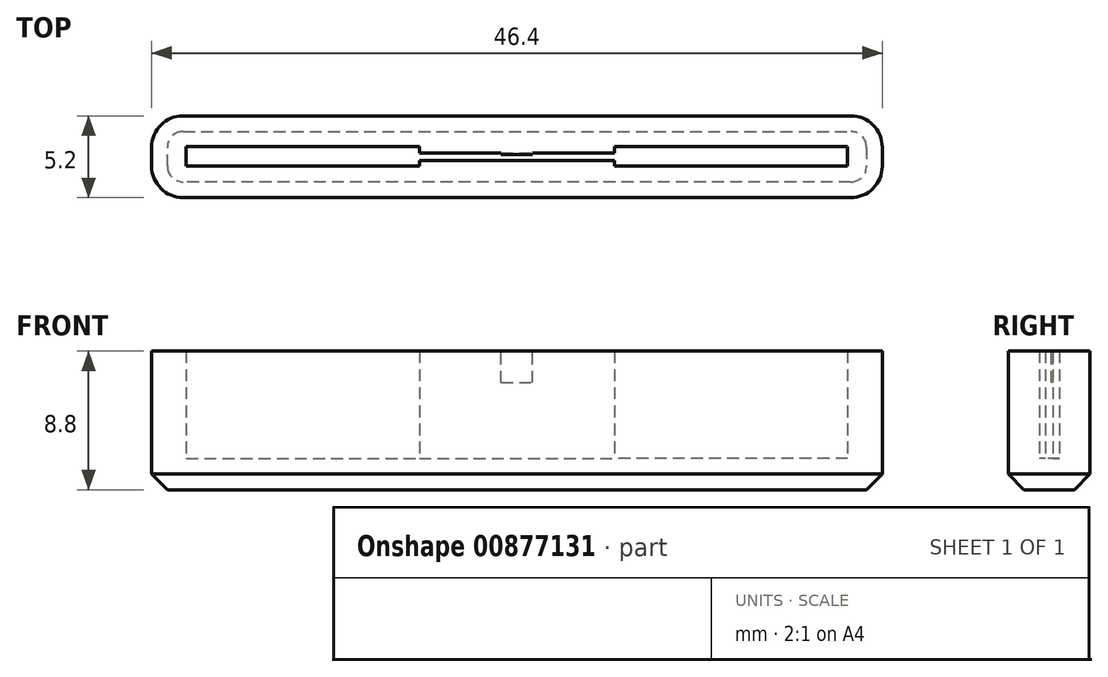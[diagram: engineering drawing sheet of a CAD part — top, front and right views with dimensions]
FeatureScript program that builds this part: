
annotation { "Feature Type Name" : "Feature", "Feature Type Description" : "" }
export const myFeature = defineFeature(function(context is Context, id is Id, definition is map)
    precondition{}
    {
        {
            var Q0;
            Q0=qCreatedBy(makeId("Top.planeOp"),FACE);
            var sketch = newSketch(context, id + "F0", { "sketchPlane" : qUnion([Q0])});
            skLineSegment(sketch, "E0.bottom", {"start": v(-23.2, 0) * mm, "end": v(23.2, 0) * mm});
            skLineSegment(sketch, "E0.top", {"start": v(-23.2, -5.2) * mm, "end": v(23.2, -5.2) * mm});
            skLineSegment(sketch, "E0.left", {"start": v(-23.2, 0) * mm, "end": v(-23.2, -5.2) * mm});
            skLineSegment(sketch, "E0.right", {"start": v(23.2, 0) * mm, "end": v(23.2, -5.2) * mm});
            skLineSegment(sketch, "E1", {"start": v(-23.2, -2.6) * mm, "end": v(23.2, -2.6) * mm, "construction": true});
            skLineSegment(sketch, "E2.left", {"start": v(-21, -2.35) * mm, "end": v(-21, -2.85) * mm});
            skLineSegment(sketch, "E2.right", {"start": v(21, -2.35) * mm, "end": v(21, -2.85) * mm});
            skPoint(sketch, "E3", {"position": v(0, -2.6) * mm});
            skLineSegment(sketch, "E4", {"start": v(0, -2.35) * mm, "end": v(0, -2.6) * mm, "construction": true});
            skLineSegment(sketch, "E5", {"start": v(0, -2.6) * mm, "end": v(0, -2.85) * mm, "construction": true});
            skLineSegment(sketch, "E6", {"start": v(-21, -2.35) * mm, "end": v(0, -2.35) * mm});
            skLineSegment(sketch, "E7", {"start": v(0, -2.35) * mm, "end": v(21, -2.35) * mm});
            skLineSegment(sketch, "E8", {"start": v(21, -2.85) * mm, "end": v(0, -2.85) * mm});
            skLineSegment(sketch, "E9", {"start": v(-21, -2.85) * mm, "end": v(0, -2.85) * mm});
            skLineSegment(sketch, "E10.bottom", {"start": v(-21, -2.35) * mm, "end": v(-6.2, -2.35) * mm});
            skLineSegment(sketch, "E10.top", {"start": v(-21, -1.94) * mm, "end": v(-6.2, -1.94) * mm});
            skLineSegment(sketch, "E10.left", {"start": v(-21, -2.35) * mm, "end": v(-21, -1.94) * mm});
            skLineSegment(sketch, "E10.right", {"start": v(-6.2, -2.35) * mm, "end": v(-6.2, -1.94) * mm});
            skLineSegment(sketch, "E11.bottom", {"start": v(-21, -2.85) * mm, "end": v(-6.2, -2.85) * mm});
            skLineSegment(sketch, "E11.top", {"start": v(-21, -3.2) * mm, "end": v(-6.2, -3.2) * mm});
            skLineSegment(sketch, "E11.left", {"start": v(-21, -2.85) * mm, "end": v(-21, -3.2) * mm});
            skLineSegment(sketch, "E11.right", {"start": v(-6.2, -2.85) * mm, "end": v(-6.2, -3.2) * mm});
            skLineSegment(sketch, "E12.MirrorCS", {"start": v(6.2, -2.35) * mm, "end": v(6.2, -1.94) * mm});
            skLineSegment(sketch, "E13.MirrorCS", {"start": v(21, -1.94) * mm, "end": v(6.2, -1.94) * mm});
            skLineSegment(sketch, "E14.MirrorCS", {"start": v(21, -2.35) * mm, "end": v(21, -1.94) * mm});
            skLineSegment(sketch, "E15.MirrorCS", {"start": v(21, -2.85) * mm, "end": v(21, -3.2) * mm});
            skLineSegment(sketch, "E16.MirrorCS", {"start": v(21, -3.2) * mm, "end": v(6.2, -3.2) * mm});
            skLineSegment(sketch, "E17.MirrorCS", {"start": v(6.2, -2.85) * mm, "end": v(6.2, -3.2) * mm});
            skSolve(sketch);
        }
        {
            var Q0;
            {var subQ4=sQuery(id+"F0.wireOp",EDGE,"E2.left");Q0=makeQuery(id+"F0.imprint","IMPRINT",FACE,{"disambiguationData":[TD([[makeQuery(id+"F0.imprint","IMPRINT",EDGE,{"derivedFrom":subQ4}),1.0]])]});}
            var Q1;
            Q1=makeQuery(id+"F0.imprint","IMPRINT",FACE,{"disambiguationData":[TD([[makeQuery(id+"F0.imprint","IMPRINT",EDGE,{"derivedFrom":sQuery(id+"F0.wireOp",EDGE,"E0.bottom")}),-1.0]])]});
            var Q2;
            Q2=makeQuery(id+"F0.imprint","IMPRINT",FACE,{"disambiguationData":[TD([[makeQuery(id+"F0.imprint","IMPRINT",EDGE,{"derivedFrom":sQuery(id+"F0.wireOp",EDGE,"E10.top")}),-1.0]])]});
            var Q3;
            Q3=makeQuery(id+"F0.imprint","IMPRINT",FACE,{"disambiguationData":[TD([[makeQuery(id+"F0.imprint","IMPRINT",EDGE,{"derivedFrom":sQuery(id+"F0.wireOp",EDGE,"E11.top")}),1.0]])]});
            var Q4;
            {var subQ0=sQuery(id+"F0.wireOp",EDGE,"E15.MirrorCS");Q4=makeQuery(id+"F0.imprint","IMPRINT",FACE,{"disambiguationData":[TD([[makeQuery(id+"F0.imprint","IMPRINT",EDGE,{"derivedFrom":subQ0}),-1.0]])]});}
            var Q5;
            {var subQ2=sQuery(id+"F0.wireOp",EDGE,"E12.MirrorCS");Q5=makeQuery(id+"F0.imprint","IMPRINT",FACE,{"disambiguationData":[TD([[makeQuery(id+"F0.imprint","IMPRINT",EDGE,{"derivedFrom":subQ2}),-1.0]])]});}
            extrude(context, id + "F1", {"entities" : qUnion([Q0, Q1, Q2, Q3, Q4, Q5]), "oppositeDirection" : true, "depth" : 2 * mm, "offsetDistance" : 25 * mm});
        }
        {
            var Q0;
            Q0=makeQuery(id+"F0.imprint","IMPRINT",FACE,{"disambiguationData":[TD([[makeQuery(id+"F0.imprint","IMPRINT",EDGE,{"derivedFrom":sQuery(id+"F0.wireOp",EDGE,"E0.bottom")}),-1.0]])]});
            extrude(context, id + "F2", {"entities" : qUnion([Q0]), "operationType" : NewBodyOperationType.ADD, "depth" : 6.8 * mm, "offsetDistance" : 25 * mm});
        }
        {
            var Q0;
            {var subQ0=sQuery(id+"F0.wireOp",EDGE,"E0.right");var subQ1=sQuery(id+"F0.wireOp",EDGE,"E0.top");Q0=makeQuery(id+"F2.boolean.opBoolean","MERGE",EDGE,{"derivedFrom":[makeQuery(id+"F1.opExtrude","SWEPT_EDGE",EDGE,{"disambiguationData":[OSD([subQ1,subQ0])]}),makeQuery(id+"F2.opExtrude","SWEPT_EDGE",EDGE,{"disambiguationData":[OSD([subQ1,subQ0])]})]});}
            var Q1;
            {var subQ0=sQuery(id+"F0.wireOp",EDGE,"E0.right");var subQ1=sQuery(id+"F0.wireOp",EDGE,"E0.bottom");Q1=makeQuery(id+"F2.boolean.opBoolean","MERGE",EDGE,{"derivedFrom":[makeQuery(id+"F1.opExtrude","SWEPT_EDGE",EDGE,{"disambiguationData":[OSD([subQ1,subQ0])]}),makeQuery(id+"F2.opExtrude","SWEPT_EDGE",EDGE,{"disambiguationData":[OSD([subQ1,subQ0])]})]});}
            var Q2;
            {var subQ0=sQuery(id+"F0.wireOp",EDGE,"E0.left");var subQ1=sQuery(id+"F0.wireOp",EDGE,"E0.top");Q2=makeQuery(id+"F2.boolean.opBoolean","MERGE",EDGE,{"derivedFrom":[makeQuery(id+"F1.opExtrude","SWEPT_EDGE",EDGE,{"disambiguationData":[OSD([subQ1,subQ0])]}),makeQuery(id+"F2.opExtrude","SWEPT_EDGE",EDGE,{"disambiguationData":[OSD([subQ1,subQ0])]})]});}
            var Q3;
            {var subQ0=sQuery(id+"F0.wireOp",EDGE,"E0.left");var subQ1=sQuery(id+"F0.wireOp",EDGE,"E0.bottom");Q3=makeQuery(id+"F2.boolean.opBoolean","MERGE",EDGE,{"derivedFrom":[makeQuery(id+"F1.opExtrude","SWEPT_EDGE",EDGE,{"disambiguationData":[OSD([subQ1,subQ0])]}),makeQuery(id+"F2.opExtrude","SWEPT_EDGE",EDGE,{"disambiguationData":[OSD([subQ1,subQ0])]})]});}
            fillet(context, id + "F3", {"entities" : qUnion([Q0, Q1, Q2, Q3]), "radius" : 2 * mm, "tangentPropagation" : true, "allowEdgeOverflow" : false});
        }
        {
            var Q0;
            Q0=makeQuery(id+"F1.opExtrude","CAP_FACE",FACE,{"disambiguationData":[OSD([sQuery(id+"F0.wireOp",EDGE,"E0.bottom"),sQuery(id+"F0.wireOp",EDGE,"E0.top"),sQuery(id+"F0.wireOp",EDGE,"E0.left"),sQuery(id+"F0.wireOp",EDGE,"E0.right")])],"isStart":false});
            chamfer(context, id + "F4", {"entities" : qUnion([Q0]), "width" : 1 * mm, "tangentPropagation" : true});
        }
        {
            var Q0;
            Q0=makeQuery(id+"F2.opExtrude","CAP_FACE",FACE,{"disambiguationData":[OSD([sQuery(id+"F0.wireOp",EDGE,"E0.bottom"),sQuery(id+"F0.wireOp",EDGE,"E0.top"),sQuery(id+"F0.wireOp",EDGE,"E0.left"),sQuery(id+"F0.wireOp",EDGE,"E0.right"),sQuery(id+"F0.wireOp",EDGE,"E2.left"),sQuery(id+"F0.wireOp",EDGE,"E2.right"),sQuery(id+"F0.wireOp",EDGE,"E6"),sQuery(id+"F0.wireOp",EDGE,"E7"),sQuery(id+"F0.wireOp",EDGE,"E8"),sQuery(id+"F0.wireOp",EDGE,"E9"),sQuery(id+"F0.wireOp",EDGE,"E10.top"),sQuery(id+"F0.wireOp",EDGE,"E10.left"),sQuery(id+"F0.wireOp",EDGE,"E10.right"),sQuery(id+"F0.wireOp",EDGE,"E11.top"),sQuery(id+"F0.wireOp",EDGE,"E11.left"),sQuery(id+"F0.wireOp",EDGE,"E11.right"),sQuery(id+"F0.wireOp",EDGE,"E12.MirrorCS"),sQuery(id+"F0.wireOp",EDGE,"E13.MirrorCS"),sQuery(id+"F0.wireOp",EDGE,"E14.MirrorCS"),sQuery(id+"F0.wireOp",EDGE,"E15.MirrorCS"),sQuery(id+"F0.wireOp",EDGE,"E16.MirrorCS"),sQuery(id+"F0.wireOp",EDGE,"E17.MirrorCS")])],"isStart":false});
            var sketch = newSketch(context, id + "F5", { "sketchPlane" : qUnion([Q0])});
            skLineSegment(sketch, "E18.bottom", {"start": v(-1, -2.35) * mm, "end": v(1, -2.35) * mm});
            skLineSegment(sketch, "E18.top", {"start": v(-1, -2.45) * mm, "end": v(1, -2.45) * mm});
            skLineSegment(sketch, "E18.left", {"start": v(-1, -2.35) * mm, "end": v(-1, -2.45) * mm});
            skLineSegment(sketch, "E18.right", {"start": v(1, -2.35) * mm, "end": v(1, -2.45) * mm});
            skSolve(sketch);
        }
        {
            var Q0;
            Q0=makeQuery(id+"F5.imprint","IMPRINT",FACE,{"disambiguationData":[TD([[makeQuery(id+"F5.imprint","IMPRINT",EDGE,{"derivedFrom":sQuery(id+"F5.wireOp",EDGE,"E18.bottom")}),-1.0]])]});
            extrude(context, id + "F6", {"entities" : qUnion([Q0]), "operationType" : NewBodyOperationType.ADD, "oppositeDirection" : true, "depth" : 2 * mm, "offsetDistance" : 25 * mm});
        }
    });
